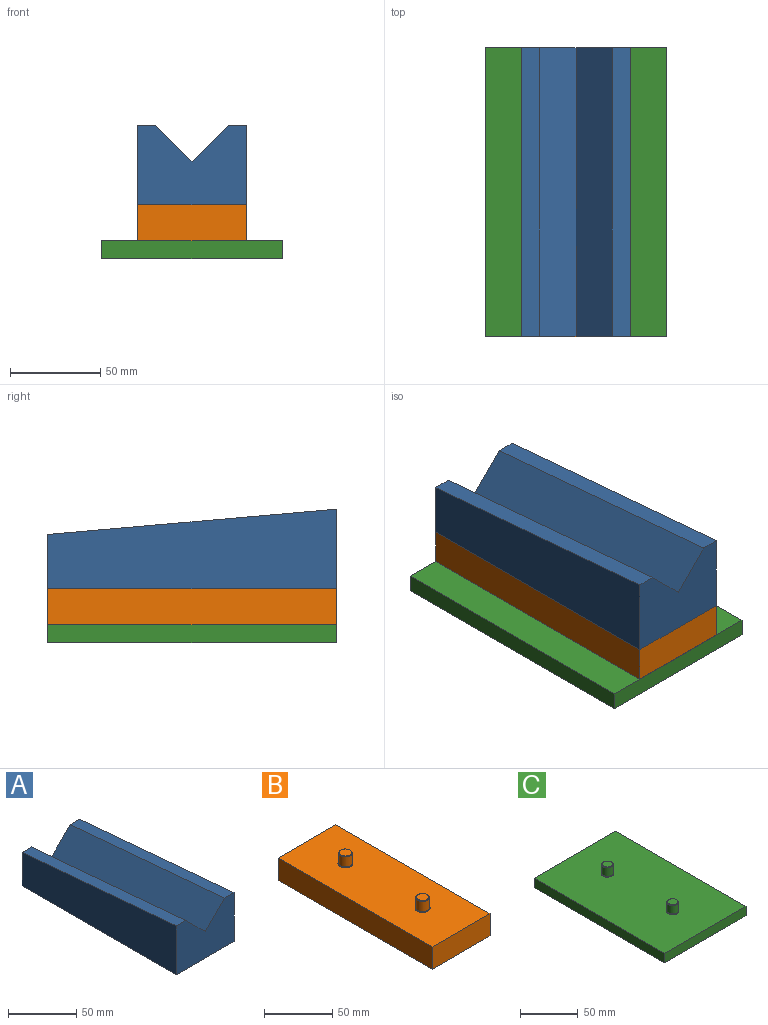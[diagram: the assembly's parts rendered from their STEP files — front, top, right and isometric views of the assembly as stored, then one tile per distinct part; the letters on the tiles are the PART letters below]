
ASSEMBLY  parts=3 mates=2
PART A: 17 faces, bbox 60x160x44 mm
  f0: plane 160x14mm, normal (0,0.09,1), area 1606.1mm2, adj f1,f2,f6,f8
  f1: plane 60x44mm, normal (0,-1,0), area 2238.4mm2, adj f0,f3,f4,f5,f6,f7,f8
  f2: plane 60x30mm, normal (0,1,0), area 1398.5mm2, adj f0,f3,f4,f5,f6,f7,f8
  f3: plane 160x60mm, normal (0,0,-1), area 9409.9mm2, adj f1,f2,f5,f6,f12,f16
  f4: plane 160x14mm, normal (0,0.09,1), area 1606.1mm2, adj f1,f2,f5,f7
  f5: plane 160x44mm, normal (1,0,0), area 5919.9mm2, adj f1,f2,f3,f4
  f6: plane 160x44mm, normal (-1,0,0), area 5919.9mm2, adj f0,f1,f2,f3
  f7: plane 160x34.07mm, normal (-0.71,0.06,0.7), area 4542.8mm2, adj f1,f2,f4,f8
  f8: plane 160x34.07mm, normal (0.71,0.06,0.7), area 4542.8mm2, adj f0,f1,f2,f7
  f9: cylinder r=5mm len=10mm, axis (0,0,-1), area 282.7mm2, adj f11,f12
  f10: plane 9x9mm, normal (0,0,-1), area 63.6mm2, adj f11
  f11: cone r=4.5mm half-angle=45deg, axis (0,0,-1), area 21.1mm2, adj f9,f10
  f12: cone r=5mm half-angle=45deg, axis (0,0,-1), area 23.3mm2, adj f3,f9
  f13: cylinder r=5mm len=10mm, axis (0,0,-1), area 282.7mm2, adj f15,f16
  f14: plane 9x9mm, normal (0,0,-1), area 63.6mm2, adj f15
  f15: cone r=5mm half-angle=45deg, axis (0,0,-1), area 21.1mm2, adj f13,f14
  f16: cone r=5.5mm half-angle=45deg, axis (0,0,-1), area 23.3mm2, adj f3,f13
PART B: 22 faces, bbox 60x160x30 mm
  f0: plane 160x20mm, normal (-1,0,0), area 3200mm2, adj f1,f3,f4,f5
  f1: plane 160x60mm, normal (0,0,-1), area 9409.9mm2, adj f0,f2,f4,f5,f9,f13
  f2: plane 160x20mm, normal (1,0,0), area 3200mm2, adj f1,f3,f4,f5
  f3: plane 160x60mm, normal (0,0,1), area 9409.9mm2, adj f0,f2,f4,f5,f16,f20
  f4: plane 60x20mm, normal (0,-1,0), area 1200mm2, adj f0,f1,f2,f3
  f5: plane 60x20mm, normal (0,1,0), area 1200mm2, adj f0,f1,f2,f3
  f6: cylinder r=5mm len=10mm, axis (0,0,-1), area 282.7mm2, adj f8,f9
  f7: plane 9x9mm, normal (0,0,-1), area 63.6mm2, adj f8
  f8: cone r=4.5mm half-angle=45deg, axis (0,0,-1), area 21.1mm2, adj f6,f7
  f9: cone r=5mm half-angle=45deg, axis (0,0,-1), area 23.3mm2, adj f1,f6
  f10: cylinder r=5mm len=10mm, axis (0,0,-1), area 282.7mm2, adj f12,f13
  f11: plane 9x9mm, normal (0,0,-1), area 63.6mm2, adj f12
  f12: cone r=5mm half-angle=45deg, axis (0,0,-1), area 21.1mm2, adj f10,f11
  f13: cone r=5.5mm half-angle=45deg, axis (0,0,-1), area 23.3mm2, adj f1,f10
  f14: cylinder r=5mm len=10mm, axis (0,0,-1), area 282.7mm2, adj f16,f17
  f15: plane 9x9mm, normal (0,0,1), area 63.6mm2, adj f17
  f16: cone r=5mm half-angle=45deg, axis (0,0,-1), area 23.3mm2, adj f3,f14
  f17: cone r=4.5mm half-angle=45deg, axis (0,0,-1), area 21.1mm2, adj f14,f15
  f18: cylinder r=5mm len=10mm, axis (0,0,-1), area 282.7mm2, adj f20,f21
  f19: plane 9x9mm, normal (0,0,1), area 63.6mm2, adj f21
  f20: cone r=5mm half-angle=45deg, axis (0,0,-1), area 23.3mm2, adj f3,f18
  f21: cone r=5mm half-angle=45deg, axis (0,0,-1), area 21.1mm2, adj f18,f19
PART C: 14 faces, bbox 100x160x20 mm
  f0: plane 160x100mm, normal (0,0,1), area 15809.9mm2, adj f1,f3,f4,f5,f8,f12
  f1: plane 160x10mm, normal (-1,0,0), area 1600mm2, adj f0,f2,f4,f5
  f2: plane 160x100mm, normal (0,0,-1), area 16000mm2, adj f1,f3,f4,f5
  f3: plane 160x10mm, normal (1,0,0), area 1600mm2, adj f0,f2,f4,f5
  f4: plane 100x10mm, normal (0,-1,0), area 1000mm2, adj f0,f1,f2,f3
  f5: plane 100x10mm, normal (0,1,0), area 1000mm2, adj f0,f1,f2,f3
  f6: cylinder r=5mm len=10mm, axis (0,0,-1), area 282.7mm2, adj f8,f9
  f7: plane 9x9mm, normal (0,0,1), area 63.6mm2, adj f9
  f8: cone r=5mm half-angle=45deg, axis (0,0,-1), area 23.3mm2, adj f0,f6
  f9: cone r=4.5mm half-angle=45deg, axis (0,0,-1), area 21.1mm2, adj f6,f7
  f10: cylinder r=5mm len=10mm, axis (0,0,-1), area 282.7mm2, adj f12,f13
  f11: plane 9x9mm, normal (0,0,1), area 63.6mm2, adj f13
  f12: cone r=5mm half-angle=45deg, axis (0,0,-1), area 23.3mm2, adj f0,f10
  f13: cone r=5mm half-angle=45deg, axis (0,0,-1), area 21.1mm2, adj f10,f11
PLACE A t=(0,0,20)mm
PLACE B at identity
PLACE C at identity fixed
MATE slider A.f9 <-> B.f6  axis (0,0,-1) through (0,40,30)mm
MATE slider B.f6 <-> C.f10  axis (0,0,-1) through (0,40,10)mm
